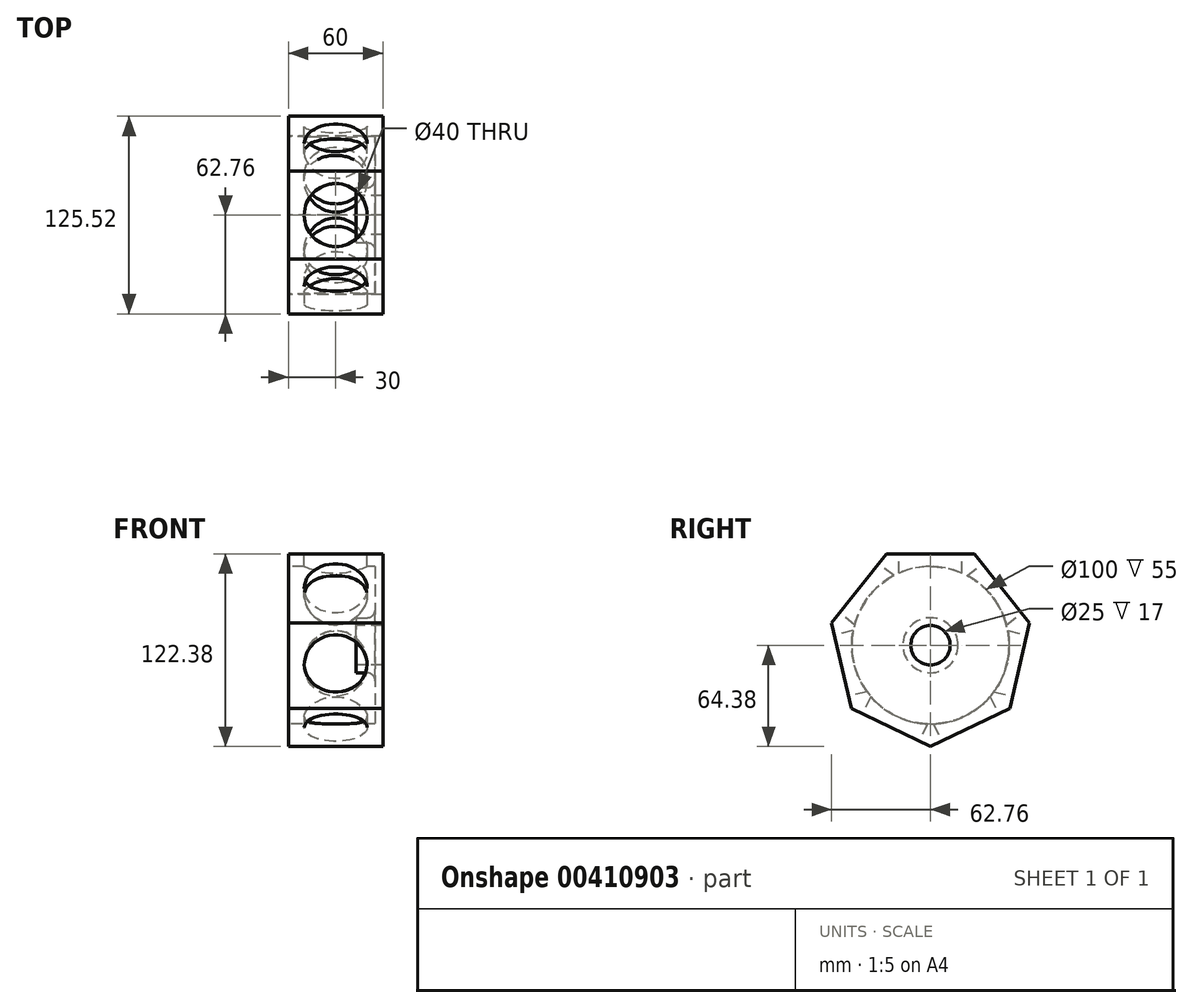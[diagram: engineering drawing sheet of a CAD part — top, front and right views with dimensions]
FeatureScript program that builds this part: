
annotation { "Feature Type Name" : "Feature", "Feature Type Description" : "" }
export const myFeature = defineFeature(function(context is Context, id is Id, definition is map)
    precondition{}
    {
        {
            var Q0;
            Q0=qCreatedBy(makeId("Right.planeOp"),FACE);
            var sketch = newSketch(context, id + "F0", { "sketchPlane" : qUnion([Q0])});
            skCircle(sketch, "E0.cCircle", {"center": v(0, 0) * mm, "radius": 64.38 * mm, "construction": true});
            skLineSegment(sketch, "E0.0", {"start": v(-27.93, 58) * mm, "end": v(27.93, 58) * mm});
            skLineSegment(sketch, "E0.1", {"start": v(27.93, 58) * mm, "end": v(62.76, 14.32) * mm});
            skLineSegment(sketch, "E0.2", {"start": v(62.76, 14.32) * mm, "end": v(50.33, -40.14) * mm});
            skLineSegment(sketch, "E0.3", {"start": v(50.33, -40.14) * mm, "end": v(0, -64.38) * mm});
            skLineSegment(sketch, "E0.4", {"start": v(0, -64.38) * mm, "end": v(-50.33, -40.14) * mm});
            skLineSegment(sketch, "E0.5", {"start": v(-50.33, -40.14) * mm, "end": v(-62.76, 14.32) * mm});
            skLineSegment(sketch, "E0.6", {"start": v(-62.76, 14.32) * mm, "end": v(-27.93, 58) * mm});
            skSolve(sketch);
        }
        {
            var Q0;
            Q0 = qSketchRegion(id + "F0", true);
            extrude(context, id + "F1", {"entities" : qUnion([Q0]), "depth" : 60 * mm});
        }
        {
            var Q0;
            Q0=makeQuery(id+"F1.opExtrude","CAP_FACE",FACE,{"disambiguationData":[OSD([sQuery(id+"F0.wireOp",EDGE,"E0.0"),sQuery(id+"F0.wireOp",EDGE,"E0.1"),sQuery(id+"F0.wireOp",EDGE,"E0.2"),sQuery(id+"F0.wireOp",EDGE,"E0.3"),sQuery(id+"F0.wireOp",EDGE,"E0.4"),sQuery(id+"F0.wireOp",EDGE,"E0.5"),sQuery(id+"F0.wireOp",EDGE,"E0.6")])],"isStart":true});
            var sketch = newSketch(context, id + "F2", { "sketchPlane" : qUnion([Q0])});
            skCircle(sketch, "E1", {"center": v(0, 0) * mm, "radius": 50 * mm});
            skSolve(sketch);
        }
        {
            var Q0;
            Q0 = qSketchRegion(id + "F2", true);
            extrude(context, id + "F3", {"entities" : qUnion([Q0]), "operationType" : NewBodyOperationType.REMOVE, "oppositeDirection" : true, "depth" : 55 * mm});
        }
        {
            var Q0;
            Q0=makeQuery(id+"F1.opExtrude","CAP_FACE",FACE,{"disambiguationData":[OSD([sQuery(id+"F0.wireOp",EDGE,"E0.0"),sQuery(id+"F0.wireOp",EDGE,"E0.1"),sQuery(id+"F0.wireOp",EDGE,"E0.2"),sQuery(id+"F0.wireOp",EDGE,"E0.3"),sQuery(id+"F0.wireOp",EDGE,"E0.4"),sQuery(id+"F0.wireOp",EDGE,"E0.5"),sQuery(id+"F0.wireOp",EDGE,"E0.6")])],"isStart":true});
            var sketch = newSketch(context, id + "F4", { "sketchPlane" : qUnion([Q0])});
            skCircle(sketch, "E2", {"center": v(0, 0) * mm, "radius": 12.5 * mm});
            skSolve(sketch);
        }
        {
            var Q0;
            Q0 = qSketchRegion(id + "F4", true);
            extrude(context, id + "F5", {"entities" : qUnion([Q0]), "operationType" : NewBodyOperationType.REMOVE, "endBound" : BoundingType.THROUGH_ALL, "oppositeDirection" : true, "depth" : 25 * mm});
        }
        {
            var Q0;
            Q0=qCreatedBy(makeId("Front.planeOp"),FACE);
            var sketch = newSketch(context, id + "F6", { "sketchPlane" : qUnion([Q0])});
            skLineSegment(sketch, "E3.top", {"start": v(43, 12.5) * mm, "end": v(55, 12.5) * mm});
            skLineSegment(sketch, "E3.left", {"start": v(43, 17.5) * mm, "end": v(43, 12.5) * mm});
            skLineSegment(sketch, "E3.right", {"start": v(55, 22.5) * mm, "end": v(55, 12.5) * mm});
            skLineSegment(sketch, "E4.bottom", {"start": v(43, 17.5) * mm, "end": v(50, 17.5) * mm});
            skArc(sketch, "E5.filletArc", {"start": v(50, 17.5) * mm, "mid": v(53.54, 18.96) * mm, "end": v(55, 22.5) * mm});
            skSolve(sketch);
        }
        {
            var Q0;
            Q0 = qSketchRegion(id + "F6", true);
            var Q1;
            Q1=makeQuery(id+"F5.boolean.opBoolean","INTERSECT",EDGE,{"derivedFrom":[makeQuery(id+"F3.boolean.opBoolean","COPY",FACE,{"derivedFrom":makeQuery(id+"F3.opExtrude","CAP_FACE",FACE,{"disambiguationData":[OSD([sQuery(id+"F2.wireOp",EDGE,"E1")])],"isStart":false})}),makeQuery(id+"F5.opExtrude","SWEPT_FACE",FACE,{"disambiguationData":[OSD([sQuery(id+"F4.wireOp",EDGE,"E2")])]})]});
            revolve(context, id + "F7", {"operationType" : NewBodyOperationType.ADD, "entities" : qUnion([Q0]), "axis" : qUnion([Q1]), "revolveType" : RevolveType.FULL});
        }
        {
            var Q0;
            Q0=makeQuery(id+"F1.opExtrude","SWEPT_FACE",FACE,{"disambiguationData":[OSD([sQuery(id+"F0.wireOp",EDGE,"E0.0")])]});
            var sketch = newSketch(context, id + "F8", { "sketchPlane" : qUnion([Q0])});
            skCircle(sketch, "E6", {"center": v(30, 0) * mm, "radius": 20 * mm});
            skSolve(sketch);
        }
        {
            var Q0;
            Q0 = qSketchRegion(id + "F8", true);
            extrude(context, id + "F9", {"entities" : qUnion([Q0]), "operationType" : NewBodyOperationType.REMOVE, "oppositeDirection" : true, "depth" : 25 * mm});
        }
        {
            var Q0;
            Q0=makeQuery(id+"F1.opExtrude","SWEPT_BODY",BODY,{"disambiguationData":[OSD([sQuery(id+"F0.wireOp",EDGE,"E0.0"),sQuery(id+"F0.wireOp",EDGE,"E0.1"),sQuery(id+"F0.wireOp",EDGE,"E0.2"),sQuery(id+"F0.wireOp",EDGE,"E0.3"),sQuery(id+"F0.wireOp",EDGE,"E0.4"),sQuery(id+"F0.wireOp",EDGE,"E0.5"),sQuery(id+"F0.wireOp",EDGE,"E0.6")])]});
            var Q1;
            Q1=makeQuery(id+"F9.boolean.opBoolean","COPY",FACE,{"derivedFrom":makeQuery(id+"F9.opExtrude","SWEPT_FACE",FACE,{"disambiguationData":[OSD([sQuery(id+"F8.wireOp",EDGE,"E6")])]})});
            var Q2;
            Q2=makeQuery(id+"F5.boolean.opBoolean","INTERSECT",EDGE,{"derivedFrom":[makeQuery(id+"F1.opExtrude","CAP_FACE",FACE,{"disambiguationData":[OSD([sQuery(id+"F0.wireOp",EDGE,"E0.0"),sQuery(id+"F0.wireOp",EDGE,"E0.1"),sQuery(id+"F0.wireOp",EDGE,"E0.2"),sQuery(id+"F0.wireOp",EDGE,"E0.3"),sQuery(id+"F0.wireOp",EDGE,"E0.4"),sQuery(id+"F0.wireOp",EDGE,"E0.5"),sQuery(id+"F0.wireOp",EDGE,"E0.6")])],"isStart":false}),makeQuery(id+"F5.opExtrude","SWEPT_FACE",FACE,{"disambiguationData":[OSD([sQuery(id+"F4.wireOp",EDGE,"E2")])]})]});
            circularPattern(context, id + "F10", {"patternType" : PatternType.FACE, "faces" : qUnion([Q1]), "axis" : qUnion([Q2]), "angle" : 360 * degree, "instanceCount" : 7, "equalSpace" : true});
        }
    });
